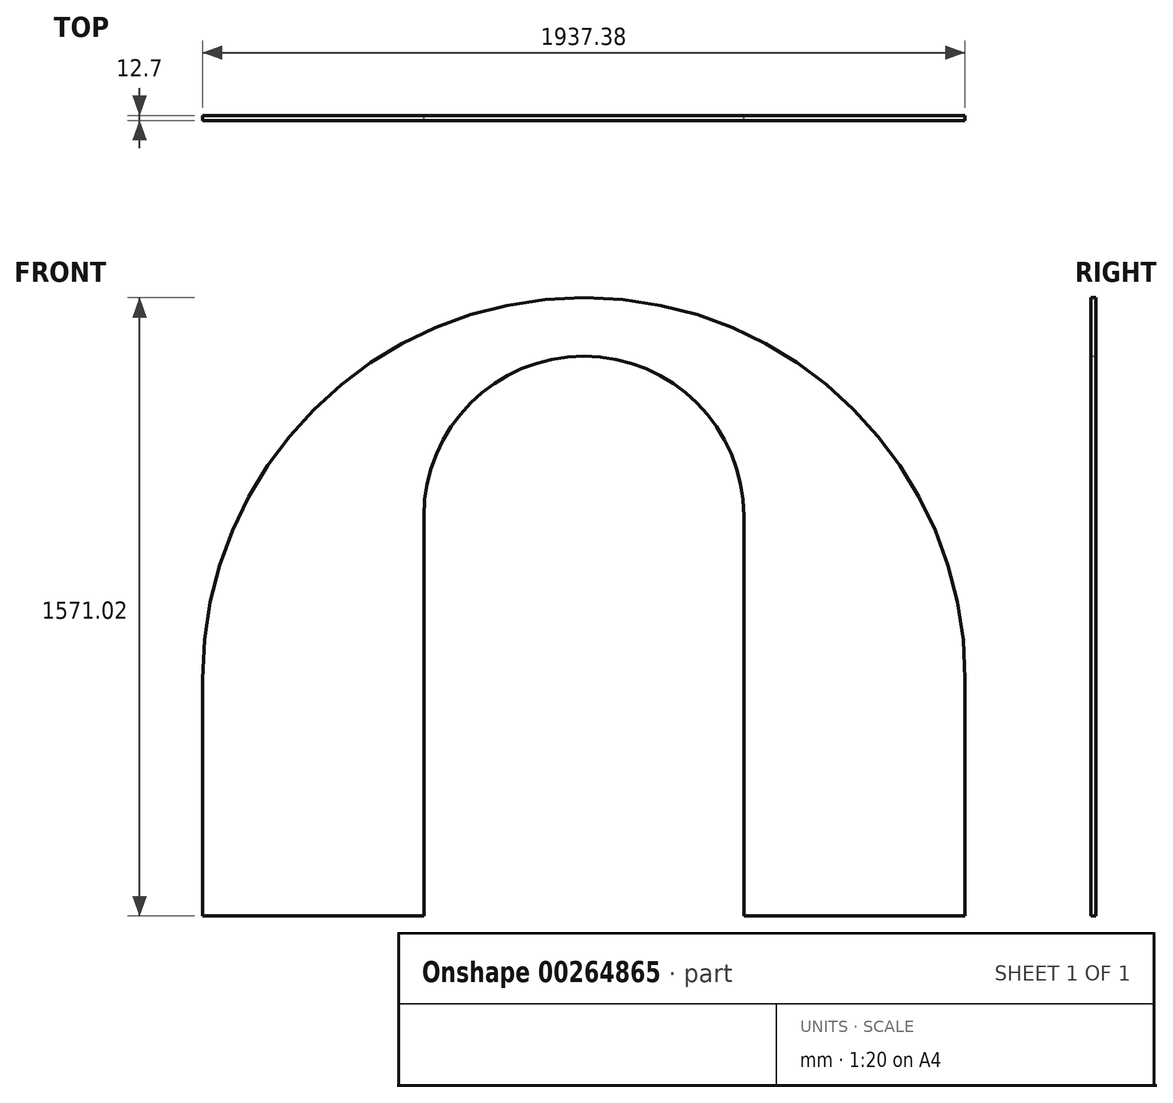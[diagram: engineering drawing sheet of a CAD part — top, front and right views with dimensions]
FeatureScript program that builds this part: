
annotation { "Feature Type Name" : "Feature", "Feature Type Description" : "" }
export const myFeature = defineFeature(function(context is Context, id is Id, definition is map)
    precondition{}
    {
        {
            var Q0;
            Q0=qCreatedBy(makeId("Front.planeOp"),FACE);
            var sketch = newSketch(context, id + "F0", { "sketchPlane" : qUnion([Q0])});
            skArc(sketch, "E0", {"start": v(968.7, 0) * mm, "mid": v(0, 968.7) * mm, "end": v(-968.7, 0) * mm});
            skArc(sketch, "E1", {"start": v(894.33, 0) * mm, "mid": v(0, 894.33) * mm, "end": v(-894.33, 0) * mm});
            skLineSegment(sketch, "E2", {"start": v(-968.7, 0) * mm, "end": v(-406.4, 0) * mm});
            skLineSegment(sketch, "E3.top", {"start": v(-968.7, -602.33) * mm, "end": v(968.7, -602.33) * mm});
            skLineSegment(sketch, "E3.left", {"start": v(-968.7, 0) * mm, "end": v(-968.7, -602.33) * mm});
            skLineSegment(sketch, "E3.right", {"start": v(968.7, 0) * mm, "end": v(968.7, -602.33) * mm});
            skLineSegment(sketch, "E4.bottom", {"start": v(0, -602.33) * mm, "end": v(-406.4, -602.33) * mm});
            skLineSegment(sketch, "E4.right", {"start": v(-406.4, -602.33) * mm, "end": v(-406.4, 413.67) * mm});
            skLineSegment(sketch, "E5.top", {"start": v(0, -602.33) * mm, "end": v(406.4, -602.33) * mm});
            skLineSegment(sketch, "E5.right", {"start": v(406.4, 413.67) * mm, "end": v(406.4, -602.33) * mm});
            skPoint(sketch, "E6.third.point.positionSnap0", {"position": v(0, 894.33) * mm});
            skArc(sketch, "E7", {"start": v(406.4, 413.67) * mm, "mid": v(0, 820.07) * mm, "end": v(-406.4, 413.67) * mm});
            skLineSegment(sketch, "E8.trimOffspring", {"start": v(406.4, 0) * mm, "end": v(968.7, 0) * mm});
            skSolve(sketch);
        }
        {
            var Q0;
            {var subQ0=sQuery(id+"F0.wireOp",EDGE,"E0");Q0=makeQuery(id+"F0.imprint","IMPRINT",FACE,{"disambiguationData":[TD([[makeQuery(id+"F0.imprint","IMPRINT",EDGE,{"derivedFrom":subQ0}),1.0]])]});}
            var Q1;
            {var subQ0=sQuery(id+"F0.wireOp",EDGE,"E3.left");Q1=makeQuery(id+"F0.imprint","IMPRINT",FACE,{"disambiguationData":[TD([[makeQuery(id+"F0.imprint","IMPRINT",EDGE,{"derivedFrom":subQ0}),1.0]])]});}
            var Q2;
            {var subQ4=sQuery(id+"F0.wireOp",EDGE,"E1");Q2=makeQuery(id+"F0.imprint","IMPRINT",FACE,{"disambiguationData":[TD([[makeQuery(id+"F0.imprint","IMPRINT",EDGE,{"derivedFrom":subQ4}),1.0]])]});}
            var Q3;
            {var subQ5=sQuery(id+"F0.wireOp",EDGE,"E3.right");Q3=makeQuery(id+"F0.imprint","IMPRINT",FACE,{"disambiguationData":[TD([[makeQuery(id+"F0.imprint","IMPRINT",EDGE,{"derivedFrom":subQ5}),-1.0]])]});}
            extrude(context, id + "F1", {"entities" : qUnion([Q0, Q1, Q2, Q3]), "depth" : 12.7 * mm, "offsetDistance" : 25.4 * mm});
        }
    });
